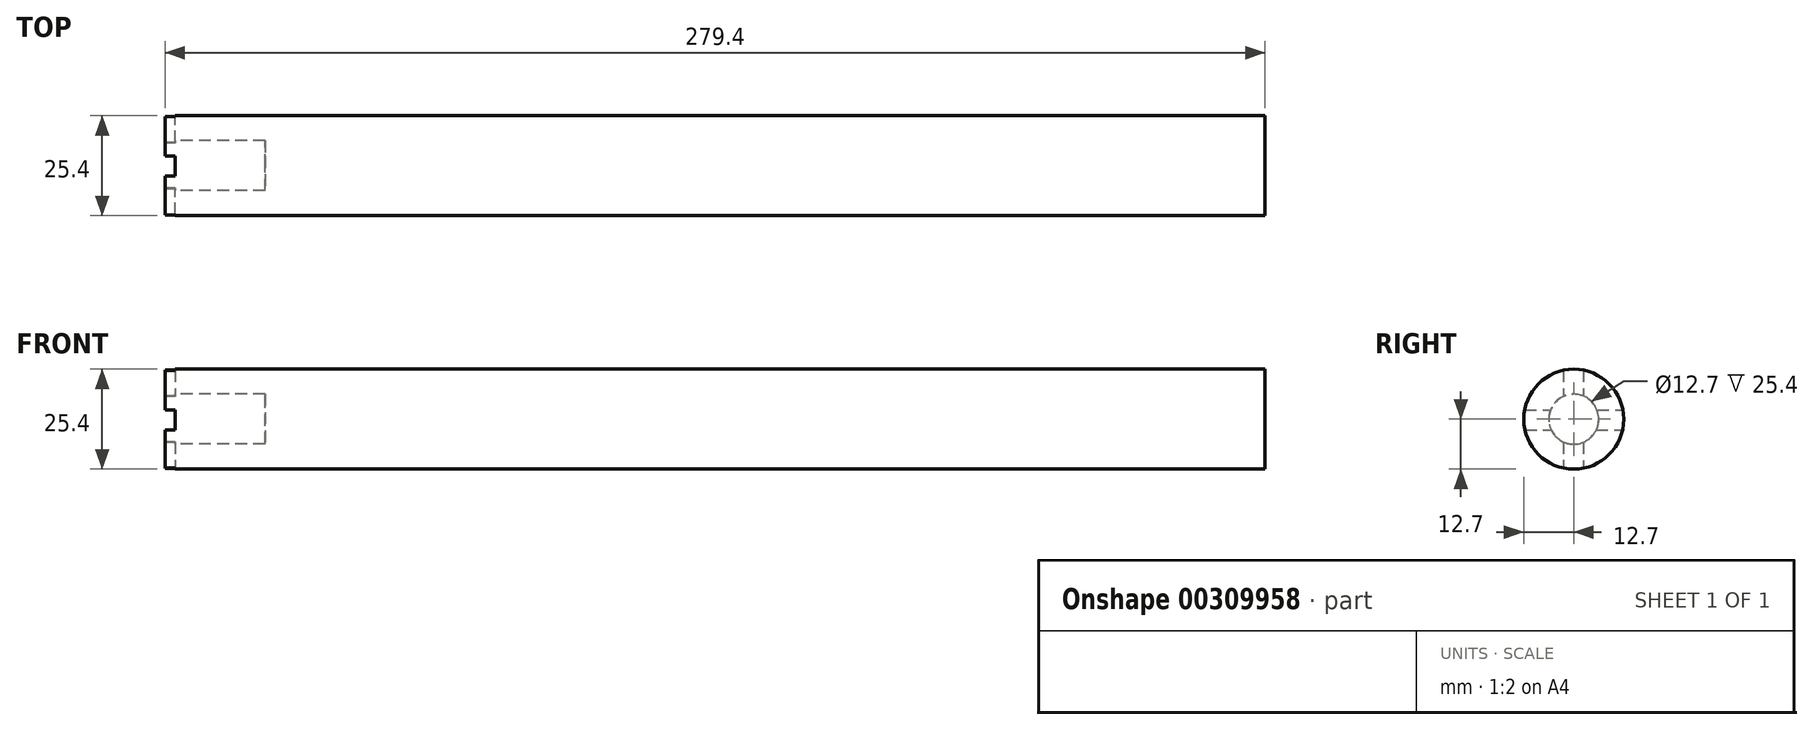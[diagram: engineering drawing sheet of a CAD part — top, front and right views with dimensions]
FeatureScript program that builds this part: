
annotation { "Feature Type Name" : "Feature", "Feature Type Description" : "" }
export const myFeature = defineFeature(function(context is Context, id is Id, definition is map)
    precondition{}
    {
        {
            var Q0;
            Q0=qCreatedBy(makeId("Front.planeOp"),FACE);
            var sketch = newSketch(context, id + "F0", { "sketchPlane" : qUnion([Q0])});
            skLineSegment(sketch, "E0.bottom", {"start": v(0, 0) * mm, "end": v(279.4, 0) * mm});
            skLineSegment(sketch, "E0.top", {"start": v(0, 25.4) * mm, "end": v(279.4, 25.4) * mm});
            skLineSegment(sketch, "E0.left", {"start": v(0, 0) * mm, "end": v(0, 25.4) * mm});
            skLineSegment(sketch, "E0.right", {"start": v(279.4, 0) * mm, "end": v(279.4, 25.4) * mm});
            skSolve(sketch);
        }
        {
            var Q0;
            Q0=makeQuery(id+"F0.imprint","IMPRINT",FACE,{"disambiguationData":[TD([[makeQuery(id+"F0.imprint","IMPRINT",EDGE,{"derivedFrom":sQuery(id+"F0.wireOp",EDGE,"E0.bottom")}),1.0]])]});
            extrude(context, id + "F1", {"entities" : qUnion([Q0]), "oppositeDirection" : true, "depth" : 25.4 * mm});
        }
        {
            var Q0;
            Q0=makeQuery(id+"F1.opExtrude","SWEPT_FACE",FACE,{"disambiguationData":[OSD([sQuery(id+"F0.wireOp",EDGE,"E0.left")])]});
            var sketch = newSketch(context, id + "F2", { "sketchPlane" : qUnion([Q0])});
            skLineSegment(sketch, "E1", {"start": v(-25.4, 12.7) * mm, "end": v(-12.7, 12.7) * mm, "construction": true});
            skCircle(sketch, "E2", {"center": v(-12.7, 12.7) * mm, "radius": 12.7 * mm});
            skSolve(sketch);
        }
        {
            var Q0;
            {var subQ0=sQuery(id+"F2.wireOp",EDGE,"E2");var subQ1=sQuery(id+"F0.wireOp",EDGE,"E0.left");var subQ4=makeQuery(id+"F1.opExtrude","CAP_EDGE",EDGE,{"disambiguationData":[OSD([subQ1])],"isStart":true});var subQ5=makeQuery(id+"F2.imprint","INTERSECT",VERTEX,{"derivedFrom":[subQ4,subQ0]});Q0=makeQuery(id+"F2.imprint","IMPRINT",FACE,{"disambiguationData":[TD([[makeQuery(id+"F2.imprint","IMPRINT",EDGE,{"disambiguationData":[TD([[subQ5,-1.0]])],"derivedFrom":subQ0}),-1.0]])]});}
            var Q1;
            {var subQ0=sQuery(id+"F2.wireOp",EDGE,"E2");var subQ1=sQuery(id+"F0.wireOp",EDGE,"E0.left");var subQ4=makeQuery(id+"F1.opExtrude","CAP_EDGE",EDGE,{"disambiguationData":[OSD([subQ1])],"isStart":false});var subQ5=makeQuery(id+"F2.imprint","INTERSECT",VERTEX,{"derivedFrom":[subQ4,subQ0]});Q1=makeQuery(id+"F2.imprint","IMPRINT",FACE,{"disambiguationData":[TD([[makeQuery(id+"F2.imprint","IMPRINT",EDGE,{"disambiguationData":[TD([[subQ5,1.0]])],"derivedFrom":subQ0}),-1.0]])]});}
            var Q2;
            {var subQ0=sQuery(id+"F2.wireOp",EDGE,"E2");var subQ1=sQuery(id+"F0.wireOp",EDGE,"E0.left");var subQ2=makeQuery(id+"F1.opExtrude","CAP_EDGE",EDGE,{"disambiguationData":[OSD([subQ1])],"isStart":false});var subQ3=makeQuery(id+"F2.imprint","INTERSECT",VERTEX,{"derivedFrom":[subQ2,subQ0]});Q2=makeQuery(id+"F2.imprint","IMPRINT",FACE,{"disambiguationData":[TD([[makeQuery(id+"F2.imprint","IMPRINT",EDGE,{"disambiguationData":[TD([[subQ3,-1.0]])],"derivedFrom":subQ0}),-1.0]])]});}
            var Q3;
            {var subQ0=sQuery(id+"F2.wireOp",EDGE,"E2");var subQ1=sQuery(id+"F0.wireOp",EDGE,"E0.left");var subQ2=makeQuery(id+"F1.opExtrude","CAP_EDGE",EDGE,{"disambiguationData":[OSD([subQ1])],"isStart":true});var subQ3=makeQuery(id+"F2.imprint","INTERSECT",VERTEX,{"derivedFrom":[subQ2,subQ0]});Q3=makeQuery(id+"F2.imprint","IMPRINT",FACE,{"disambiguationData":[TD([[makeQuery(id+"F2.imprint","IMPRINT",EDGE,{"disambiguationData":[TD([[subQ3,1.0]])],"derivedFrom":subQ0}),-1.0]])]});}
            extrude(context, id + "F3", {"entities" : qUnion([Q0, Q1, Q2, Q3]), "operationType" : NewBodyOperationType.REMOVE, "oppositeDirection" : true, "depth" : 279.4 * mm});
        }
        {
            var Q0;
            Q0=qCreatedBy(makeId("Right.planeOp"),FACE);
            var sketch = newSketch(context, id + "F4", { "sketchPlane" : qUnion([Q0])});
            skLineSegment(sketch, "E3", {"start": v(0, 0) * mm, "end": v(12.7, 0) * mm, "construction": true});
            skLineSegment(sketch, "E4", {"start": v(12.7, 0) * mm, "end": v(12.7, 12.7) * mm, "construction": true});
            skCircle(sketch, "E5", {"center": v(12.7, 12.7) * mm, "radius": 6.35 * mm});
            skSolve(sketch);
        }
        {
            var Q0;
            Q0=makeQuery(id+"F4.imprint","IMPRINT",FACE,{"disambiguationData":[TD([[makeQuery(id+"F4.imprint","IMPRINT",EDGE,{"derivedFrom":sQuery(id+"F4.wireOp",EDGE,"E5")}),1.0]])]});
            var Q1;
            Q1=sQuery(id+"F4.wireOp",EDGE,"E5");
            extrude(context, id + "F5", {"entities" : qUnion([Q0]), "operationType" : NewBodyOperationType.REMOVE, "surfaceEntities" : qUnion([Q1]), "depth" : 25.4 * mm});
        }
        {
            var Q0;
            {var subQ0=sQuery(id+"F2.wireOp",EDGE,"E2");var subQ1=sQuery(id+"F0.wireOp",EDGE,"E0.left");var subQ3=makeQuery(id+"F2.imprint","INTERSECT",VERTEX,{"derivedFrom":[makeQuery(id+"F1.opExtrude","CAP_EDGE",EDGE,{"disambiguationData":[OSD([subQ1])],"isStart":true}),subQ0]});Q0=makeQuery(id+"F2.imprint","IMPRINT",FACE,{"disambiguationData":[TD([[makeQuery(id+"F2.imprint","IMPRINT",EDGE,{"disambiguationData":[TD([[subQ3,-1.0]])],"derivedFrom":subQ0}),1.0]])]});}
            var sketch = newSketch(context, id + "F6", { "sketchPlane" : qUnion([Q0])});
            skLineSegment(sketch, "E6.bottom", {"start": v(-10.08, 35.87) * mm, "end": v(-15.16, 35.87) * mm});
            skLineSegment(sketch, "E6.top", {"start": v(-10.08, -10.97) * mm, "end": v(-15.16, -10.97) * mm});
            skLineSegment(sketch, "E6.left", {"start": v(-10.08, 35.87) * mm, "end": v(-10.08, -10.97) * mm});
            skLineSegment(sketch, "E6.right", {"start": v(-15.16, 35.87) * mm, "end": v(-15.16, -10.97) * mm});
            skPoint(sketch, "E6.middle", {"position": v(-12.62, 12.45) * mm});
            skLineSegment(sketch, "E7.bottom", {"start": v(36.61, 14.99) * mm, "end": v(-61.86, 14.99) * mm});
            skLineSegment(sketch, "E7.top", {"start": v(36.61, 9.9) * mm, "end": v(-61.86, 9.9) * mm});
            skLineSegment(sketch, "E7.left", {"start": v(36.61, 14.99) * mm, "end": v(36.61, 9.9) * mm});
            skLineSegment(sketch, "E7.right", {"start": v(-61.86, 14.99) * mm, "end": v(-61.86, 9.9) * mm});
            skSolve(sketch);
        }
        {
            var Q0;
            Q0 = qSketchRegion(id + "F6", true);
            extrude(context, id + "F7", {"entities" : qUnion([Q0]), "operationType" : NewBodyOperationType.REMOVE, "oppositeDirection" : true, "depth" : 2.54 * mm});
        }
    });
